# Revit family: FERN_VIZULO
name_source: partatom
category: Lighting Fixtures
units: mm (PartAtom-declared; Revit-internal decimal feet)

## family parameters
Always vertical = Yes
Cut with Voids When Loaded = No
Light Source = Yes
OmniClass Number = 23.80.70.00
OmniClass Title = Lighting
Part Type = Normal
Room Calculation Point = No
Round Connector Dimension = Use Diameter
Shared = No
Work Plane-Based = No

## types (40) — shared parameters
Color Filter = 16777215
Dimming Lamp Color Temperature Shift = <None>
Light Source Symbol Size = 577 mm  [stored 1.89304 ft]
zero-valued in all types: Default Elevation

## per-type parameters (varying)
| type | Emit from Line Length |
| 21 W, 600 mm, 3000 K | 576 mm  [stored 1.88976 ft] |
| 21 W, 600 mm, 4000 K | 576 mm  [stored 1.88976 ft] |
| 30 W, 600 mm, 3000 K | 576 mm  [stored 1.88976 ft] |
| 30 W, 600 mm, 4000 K | 576 mm  [stored 1.88976 ft] |
| 22 W, 600 mm, 3000 K | 576 mm  [stored 1.88976 ft] |
| 22 W, 600 mm, 4000 K | 576 mm  [stored 1.88976 ft] |
| 31 W, 600 mm, 3000 K | 576 mm  [stored 1.88976 ft] |
| 31 W, 600 mm, 4000 K | 577 mm  [stored 1.89304 ft] |
| 24 W, 600 mm, 3000 K | 576 mm  [stored 1.88976 ft] |
| 24 W, 600 mm, 4000 K | 576 mm  [stored 1.88976 ft] |
| 34 W, 1200 mm, 3000 K | 1177 mm  [stored 3.86155 ft] |
| 39 W, 1200 mm, 3000 K | 1177 mm  [stored 3.86155 ft] |
| 61 W, 1200 mm, 3000 K | 1177 mm  [stored 3.86155 ft] |
| 61 W, 1200 mm, 4000 K | 1177 mm  [stored 3.86155 ft] |
| 60 W, 1200 mm, 3000 K | 1177 mm  [stored 3.86155 ft] |
| 60 W, 1200 mm, 4000 K | 1177 mm  [stored 3.86155 ft] |
| 31 W, 1200 mm, 3000 K | 1177 mm  [stored 3.86155 ft] |
| 31 W, 1200 mm, 4000 K | 1177 mm  [stored 3.86155 ft] |
| 32 W, 1200 mm, 3000 K | 1177 mm  [stored 3.86155 ft] |
| 32 W, 1200 mm, 4000 K | 1177 mm  [stored 3.86155 ft] |
| 37 W, 1200 mm, 3000 K | 1177 mm  [stored 3.86155 ft] |
| 37 W, 1200 mm, 4000 K | 1177 mm  [stored 3.86155 ft] |
| 38 W, 1200 mm, 3000 K | 1177 mm  [stored 3.86155 ft] |
| 38 W, 1200 mm, 4000 K | 1177 mm  [stored 3.86155 ft] |
| 45 W, 1200 mm, 3000 K | 1177 mm  [stored 3.86155 ft] |
| 45 W, 1200 mm, 4000 K | 1177 mm  [stored 3.86155 ft] |
| 46 W, 1200 mm, 3000 K | 1177 mm  [stored 3.86155 ft] |
| 46 W, 1200 mm, 4000 K | 1177 mm  [stored 3.86155 ft] |
| 42 W, 1500 mm, 3000 K | 1477 mm  [stored 4.8458 ft] |
| 42 W, 1500 mm, 4000 K | 1477 mm  [stored 4.8458 ft] |
| 58 W, 1500 mm, 3000 K | 1477 mm  [stored 4.8458 ft] |
| 58 W, 1500 mm, 4000 K | 1477 mm  [stored 4.8458 ft] |
| 75 W, 1500 mm, 3000 K | 1477 mm  [stored 4.8458 ft] |
| 75 W, 1500 mm, 4000 K | 1477 mm  [stored 4.8458 ft] |
| 43 W, 1500 mm, 3000 K | 1477 mm  [stored 4.8458 ft] |
| 43 W, 1500 mm, 4000 K | 1477 mm  [stored 4.8458 ft] |
| 59 W, 1500 mm, 3000 K | 1477 mm  [stored 4.8458 ft] |
| 59 W, 1500 mm, 4000 K | 1477 mm  [stored 4.8458 ft] |
| 76 W, 1500 mm, 3000 K | 1477 mm  [stored 4.8458 ft] |
| 76 W, 1500 mm, 4000 K | 1477 mm  [stored 4.8458 ft] |

note: [stored X ft] marks values corroborated as IEEE doubles in the binary element streams (Revit-internal decimal feet)

## geometry (parser evidence)
native form markers: Sweep x3
no freeform markers — native parametric forms only
